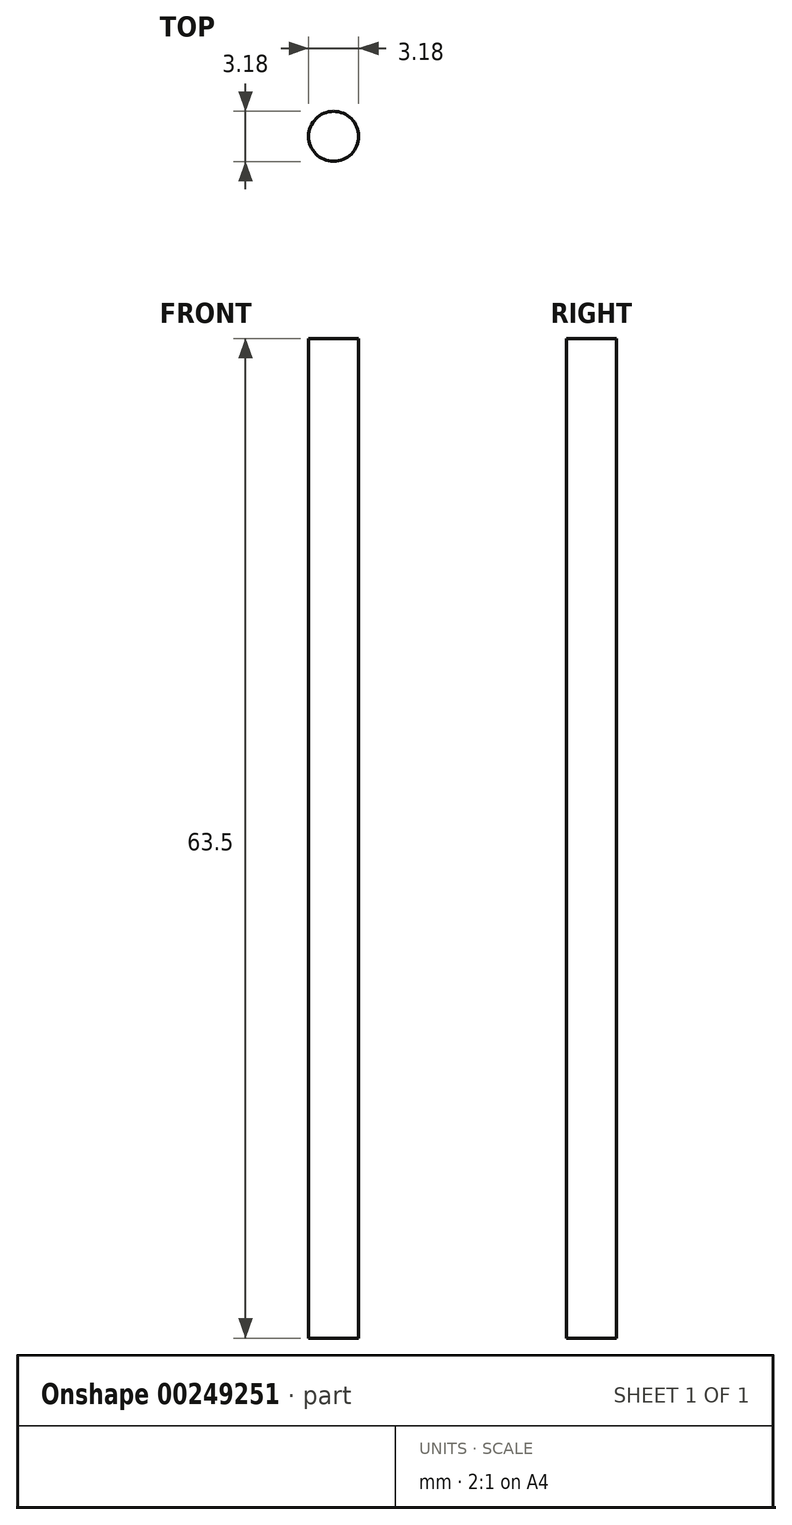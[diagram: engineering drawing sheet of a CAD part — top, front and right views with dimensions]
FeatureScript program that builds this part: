
annotation { "Feature Type Name" : "Feature", "Feature Type Description" : "" }
export const myFeature = defineFeature(function(context is Context, id is Id, definition is map)
    precondition{}
    {
        {
            var Q0;
            Q0=qCreatedBy(makeId("Top.planeOp"),FACE);
            var sketch = newSketch(context, id + "F0", { "sketchPlane" : qUnion([Q0])});
            skCircle(sketch, "E0", {"center": v(0, 0) * mm, "radius": 1.59 * mm});
            skSolve(sketch);
        }
        {
            var Q0;
            Q0=makeQuery(id+"F0.imprint","IMPRINT",FACE,{"disambiguationData":[TD([[makeQuery(id+"F0.imprint","IMPRINT",EDGE,{"derivedFrom":sQuery(id+"F0.wireOp",EDGE,"E0")}),1.0]])]});
            extrude(context, id + "F1", {"entities" : qUnion([Q0]), "depth" : 63.5 * mm});
        }
    });
